# Revit family: bathtub (426)
name_source: partatom
category: Plumbing Fixtures
units: mm (PartAtom-declared; Revit-internal decimal feet)

## family parameters
Always vertical = Yes
Cut with Voids When Loaded = No
OmniClass Number = 23.45.05.14.21.17
OmniClass Title = Therapeutic Whirlpool Baths
Part Type = Normal
Room Calculation Point = No
Round Connector Dimension = Use Radius
Shared = No
Work Plane-Based = No

## types (1)
- 7236
    Air Jets = Yes
    Apparent Load = 0 VA
    Assembly Code = D2010510
    CW Connection = No
    CWFU = 0
    Capacity = 50
    Connector Description = ELECTRICAL CONNECTOR
    Country = UNITED STATES
    Default Elevation = 0' - 0"
    Description = THERAPEUTIC BATH
    Drain Connector Description = SANITARY WASTE DRAIN
    Drain Diameter = 0' - 3"
    Drain Radius = 0' - 1 1/2"
    HW Connection = No
    HWFU = 0
    Height = 1' - 9"
    Length = 6' - 0"
    Lens Material = Polycarbonate - BainUltra - Clear
    Manufacturer = BAINULTRA
    Model = 7236
    Number of Poles = 1
    Other Region = No
    Power Factor = 1
    Product Documentation Link = http://www.bainultra.com
    Product Name = AMMA
    Product Page URL = http://www.bainultra.com
    Region = NORTH AMERICA
    Series = AMMA
    Shipping Weight = 158.00 lb
    URL = http://www.bainultra.com
    US Region = Yes
    Vent Connection = No
    Voltage = 0 V
    WFU = 4
    Waste Connection = No
    Width = 3' - 0"

## geometry (parser evidence)
native form markers: Blend x4, Sweep x15
no freeform markers — native parametric forms only
